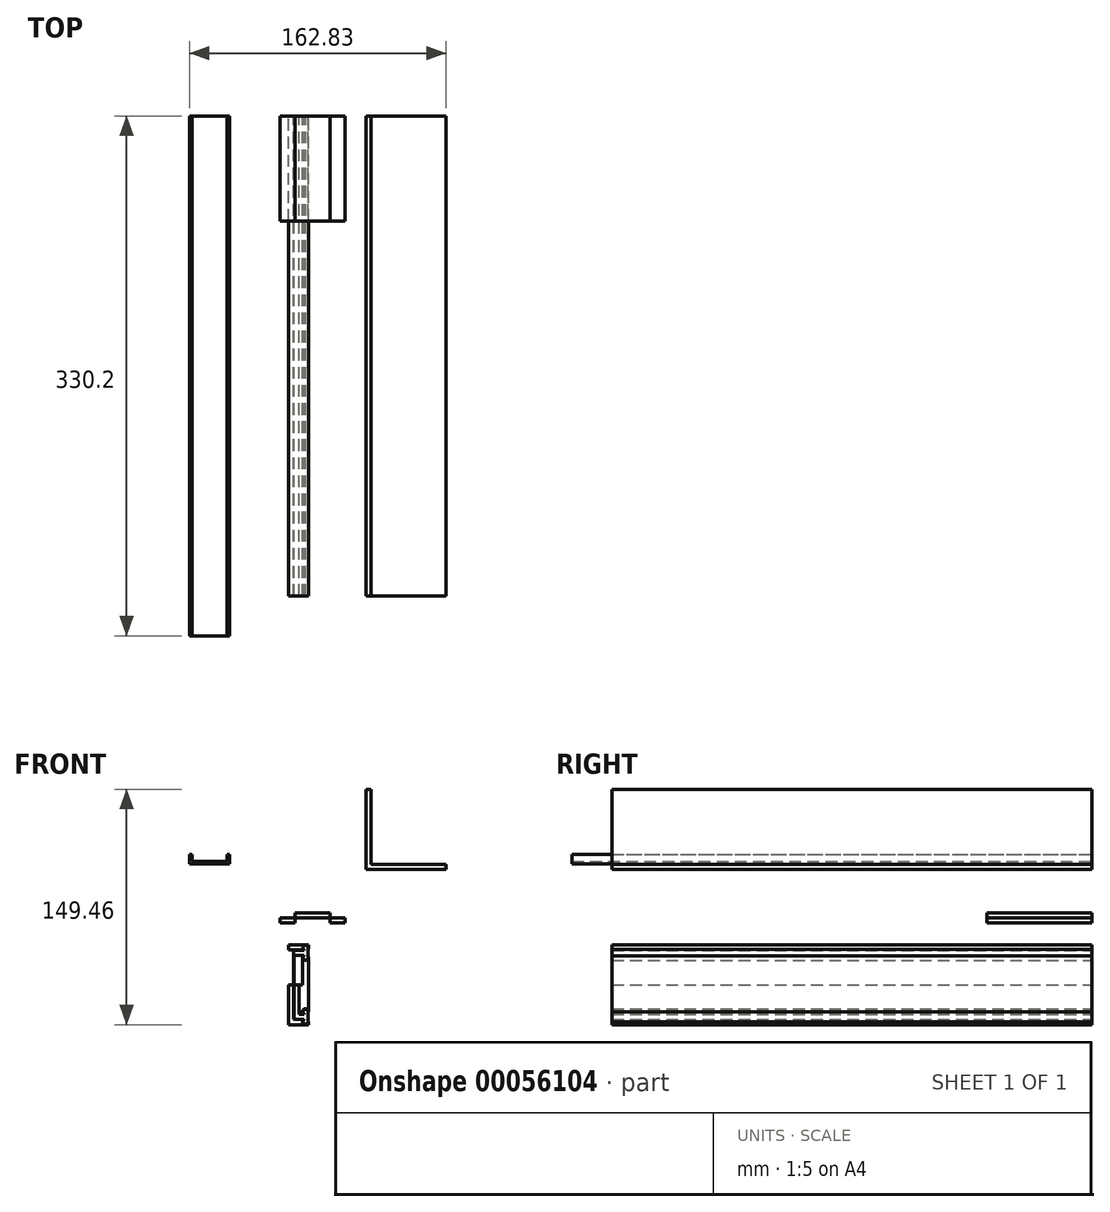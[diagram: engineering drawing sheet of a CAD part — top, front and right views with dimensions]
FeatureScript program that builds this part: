
annotation { "Feature Type Name" : "Feature", "Feature Type Description" : "" }
export const myFeature = defineFeature(function(context is Context, id is Id, definition is map)
    precondition{}
    {
        {
            var Q0;
            Q0=qCreatedBy(makeId("Front.planeOp"),FACE);
            var sketch = newSketch(context, id + "F0", { "sketchPlane" : qUnion([Q0])});
            skLineSegment(sketch, "E0.rect.bottom", {"start": v(20.64, 1.59) * mm, "end": v(-20.64, 1.59) * mm});
            skLineSegment(sketch, "E0.rect.top", {"start": v(20.64, -1.59) * mm, "end": v(-20.64, -1.59) * mm});
            skLineSegment(sketch, "E0.rect.left", {"start": v(20.64, 1.59) * mm, "end": v(20.64, -1.59) * mm});
            skLineSegment(sketch, "E0.rect.right", {"start": v(-20.64, 1.59) * mm, "end": v(-20.64, -1.59) * mm});
            skPoint(sketch, "E0.rect.middle", {"position": v(0, 0) * mm});
            skLineSegment(sketch, "E1.rect.bottom", {"start": v(11.11, 4.76) * mm, "end": v(-11.11, 4.76) * mm});
            skLineSegment(sketch, "E1.rect.top", {"start": v(11.11, -1.59) * mm, "end": v(-11.11, -1.59) * mm});
            skLineSegment(sketch, "E1.rect.left", {"start": v(11.11, 4.76) * mm, "end": v(11.11, -1.59) * mm});
            skLineSegment(sketch, "E1.rect.right", {"start": v(-11.11, 4.76) * mm, "end": v(-11.11, -1.59) * mm});
            skPoint(sketch, "E1.rect.middle", {"position": v(0, 1.59) * mm});
            skSolve(sketch);
        }
        {
            var Q0;
            {var subQ5=sQuery(id+"F0.wireOp",EDGE,"E1.rect.bottom");Q0=makeQuery(id+"F0.imprint","IMPRINT",FACE,{"disambiguationData":[TD([[makeQuery(id+"F0.imprint","IMPRINT",EDGE,{"derivedFrom":subQ5}),1.0]])]});}
            var Q1;
            {var subQ5=sQuery(id+"F0.wireOp",EDGE,"E1.rect.top");Q1=makeQuery(id+"F0.imprint","IMPRINT",FACE,{"disambiguationData":[TD([[makeQuery(id+"F0.imprint","IMPRINT",EDGE,{"derivedFrom":subQ5}),-1.0]])]});}
            var Q2;
            {var subQ0=sQuery(id+"F0.wireOp",EDGE,"E0.rect.right");Q2=makeQuery(id+"F0.imprint","IMPRINT",FACE,{"disambiguationData":[TD([[makeQuery(id+"F0.imprint","IMPRINT",EDGE,{"derivedFrom":subQ0}),1.0]])]});}
            var Q3;
            {var subQ0=sQuery(id+"F0.wireOp",EDGE,"E0.rect.left");Q3=makeQuery(id+"F0.imprint","IMPRINT",FACE,{"disambiguationData":[TD([[makeQuery(id+"F0.imprint","IMPRINT",EDGE,{"derivedFrom":subQ0}),-1.0]])]});}
            extrude(context, id + "F1", {"entities" : qUnion([Q0, Q1, Q2, Q3]), "depth" : 66.67 * mm});
        }
        {
            var Q0;
            Q0=qCreatedBy(makeId("Front.planeOp"),FACE);
            var sketch = newSketch(context, id + "F2", { "sketchPlane" : qUnion([Q0])});
            skLineSegment(sketch, "E2.rect.bottom", {"start": v(-52.61, 35.78) * mm, "end": v(-78.01, 35.78) * mm});
            skLineSegment(sketch, "E2.rect.top", {"start": v(-52.61, 41.77) * mm, "end": v(-78.01, 41.77) * mm});
            skLineSegment(sketch, "E2.rect.left", {"start": v(-52.61, 35.78) * mm, "end": v(-52.61, 41.77) * mm});
            skLineSegment(sketch, "E2.rect.right", {"start": v(-78.01, 35.78) * mm, "end": v(-78.01, 41.77) * mm});
            skPoint(sketch, "E2.rect.middle", {"position": v(-65.31, 38.77) * mm});
            skLineSegment(sketch, "E3.rect.bottom", {"start": v(-76.42, 37.36) * mm, "end": v(-54.2, 37.36) * mm});
            skLineSegment(sketch, "E3.rect.top", {"start": v(-76.42, 46.18) * mm, "end": v(-54.2, 46.18) * mm});
            skLineSegment(sketch, "E3.rect.left", {"start": v(-76.42, 37.36) * mm, "end": v(-76.42, 46.18) * mm});
            skLineSegment(sketch, "E3.rect.right", {"start": v(-54.2, 37.36) * mm, "end": v(-54.2, 46.18) * mm});
            skPoint(sketch, "E3.rect.middle", {"position": v(-65.31, 41.77) * mm});
            skSolve(sketch);
        }
        {
            var Q0;
            Q0=makeQuery(id+"F2.imprint","IMPRINT",FACE,{"disambiguationData":[TD([[makeQuery(id+"F2.imprint","IMPRINT",EDGE,{"derivedFrom":sQuery(id+"F2.wireOp",EDGE,"E2.rect.bottom")}),-1.0]])]});
            extrude(context, id + "F3", {"entities" : qUnion([Q0]), "depth" : 330.2 * mm});
        }
        {
            var Q0;
            Q0=qCreatedBy(makeId("Front.planeOp"),FACE);
            var sketch = newSketch(context, id + "F4", { "sketchPlane" : qUnion([Q0])});
            skLineSegment(sketch, "E4.bottom", {"start": v(34.02, 32.27) * mm, "end": v(84.82, 32.27) * mm});
            skLineSegment(sketch, "E4.top", {"start": v(34.02, 83.07) * mm, "end": v(84.82, 83.07) * mm});
            skLineSegment(sketch, "E4.left", {"start": v(34.02, 32.27) * mm, "end": v(34.02, 83.07) * mm});
            skLineSegment(sketch, "E4.right", {"start": v(84.82, 32.27) * mm, "end": v(84.82, 83.07) * mm});
            skLineSegment(sketch, "E5.bottom", {"start": v(37.2, 35.44) * mm, "end": v(84.82, 35.44) * mm});
            skLineSegment(sketch, "E5.top", {"start": v(37.2, 83.07) * mm, "end": v(84.82, 83.07) * mm});
            skLineSegment(sketch, "E5.left", {"start": v(37.2, 35.44) * mm, "end": v(37.2, 83.07) * mm});
            skLineSegment(sketch, "E5.right", {"start": v(84.82, 35.44) * mm, "end": v(84.82, 83.07) * mm});
            skSolve(sketch);
        }
        {
            var Q0;
            Q0=makeQuery(id+"F4.imprint","IMPRINT",FACE,{"disambiguationData":[TD([[makeQuery(id+"F4.imprint","IMPRINT",EDGE,{"derivedFrom":sQuery(id+"F4.wireOp",EDGE,"E4.bottom")}),1.0]])]});
            extrude(context, id + "F5", {"entities" : qUnion([Q0]), "depth" : 304.8 * mm});
        }
        {
            var Q0;
            Q0=qCreatedBy(makeId("Front.planeOp"),FACE);
            var sketch = newSketch(context, id + "F6", { "sketchPlane" : qUnion([Q0])});
            skLineSegment(sketch, "E6", {"start": v(0, -40.99) * mm, "end": v(-21.53, -40.99) * mm, "construction": true});
            skCircle(sketch, "E7", {"center": v(-4.4, -17.5) * mm, "radius": 1.59 * mm});
            skCircle(sketch, "E8", {"center": v(-4.4, -23.84) * mm, "radius": 1.59 * mm});
            skCircle(sketch, "E9", {"center": v(-4.4, -17.5) * mm, "radius": 1.9 * mm});
            skCircle(sketch, "E10", {"center": v(-4.4, -23.84) * mm, "radius": 1.9 * mm});
            skLineSegment(sketch, "E11.bottom", {"start": v(-2.5, -15.59) * mm, "end": v(-15.2, -15.59) * mm});
            skLineSegment(sketch, "E11.top", {"start": v(-2.5, -40.99) * mm, "end": v(-15.2, -40.99) * mm});
            skLineSegment(sketch, "E11.left", {"start": v(-2.5, -15.59) * mm, "end": v(-2.5, -40.99) * mm});
            skLineSegment(sketch, "E11.right", {"start": v(-15.2, -15.59) * mm, "end": v(-15.2, -40.99) * mm});
            skLineSegment(sketch, "E12", {"start": v(-5.82, -18.76) * mm, "end": v(-15.2, -18.76) * mm});
            skLineSegment(sketch, "E13", {"start": v(-15.2, -18.76) * mm, "end": v(-12.02, -18.76) * mm});
            skLineSegment(sketch, "E14", {"start": v(-12.02, -18.76) * mm, "end": v(-12.02, -40.99) * mm});
            skLineSegment(sketch, "E15", {"start": v(-5.45, -19.08) * mm, "end": v(-12.02, -19.08) * mm});
            skLineSegment(sketch, "E16", {"start": v(-12.02, -19.08) * mm, "end": v(-11.7, -19.08) * mm});
            skLineSegment(sketch, "E17", {"start": v(-11.7, -19.08) * mm, "end": v(-11.7, -40.99) * mm});
            skLineSegment(sketch, "E18", {"start": v(-5.45, -22.25) * mm, "end": v(-11.7, -22.25) * mm});
            skLineSegment(sketch, "E19", {"start": v(-11.7, -22.25) * mm, "end": v(-8.53, -22.25) * mm});
            skLineSegment(sketch, "E20", {"start": v(-8.53, -22.25) * mm, "end": v(-8.53, -40.99) * mm});
            skLineSegment(sketch, "E21", {"start": v(-6.3, -23.84) * mm, "end": v(-6.3, -40.99) * mm});
            skLineSegment(sketch, "E22", {"start": v(-2.5, -23.84) * mm, "end": v(-2.5, -40.99) * mm});
            skLineSegment(sketch, "E23.bottom", {"start": v(-5.45, -17.5) * mm, "end": v(-2.81, -17.5) * mm});
            skLineSegment(sketch, "E23.top", {"start": v(-5.45, -23.84) * mm, "end": v(-2.81, -23.84) * mm});
            skLineSegment(sketch, "E23.left", {"start": v(-5.45, -17.5) * mm, "end": v(-5.45, -23.84) * mm});
            skLineSegment(sketch, "E23.right", {"start": v(-2.81, -17.5) * mm, "end": v(-2.81, -23.84) * mm});
            skLineSegment(sketch, "E24.MirrorCS", {"start": v(-12.02, -62.9) * mm, "end": v(-11.7, -62.9) * mm});
            skLineSegment(sketch, "E25.MirrorCS", {"start": v(-2.5, -58.13) * mm, "end": v(-2.5, -40.99) * mm});
            skLineSegment(sketch, "E26.MirrorCS", {"start": v(-11.7, -59.72) * mm, "end": v(-8.53, -59.72) * mm});
            skLineSegment(sketch, "E27.MirrorCS", {"start": v(-2.81, -64.48) * mm, "end": v(-2.81, -58.13) * mm});
            skLineSegment(sketch, "E28.MirrorCS", {"start": v(-5.45, -62.9) * mm, "end": v(-12.02, -62.9) * mm});
            skLineSegment(sketch, "E29.MirrorCS", {"start": v(-12.02, -63.21) * mm, "end": v(-12.02, -40.99) * mm});
            skLineSegment(sketch, "E30.MirrorCS", {"start": v(-15.2, -63.21) * mm, "end": v(-12.02, -63.21) * mm});
            skLineSegment(sketch, "E31.MirrorCS", {"start": v(-8.53, -59.72) * mm, "end": v(-8.53, -40.99) * mm});
            skLineSegment(sketch, "E32.MirrorCS", {"start": v(-5.82, -63.21) * mm, "end": v(-15.2, -63.21) * mm});
            skLineSegment(sketch, "E33.MirrorCS", {"start": v(-5.45, -58.13) * mm, "end": v(-2.81, -58.13) * mm});
            skLineSegment(sketch, "E34.MirrorCS", {"start": v(-15.2, -66.39) * mm, "end": v(-15.2, -40.99) * mm});
            skLineSegment(sketch, "E35.MirrorCS", {"start": v(-6.3, -58.13) * mm, "end": v(-6.3, -40.99) * mm});
            skLineSegment(sketch, "E36.MirrorCS", {"start": v(-2.5, -66.39) * mm, "end": v(-2.5, -40.99) * mm});
            skLineSegment(sketch, "E37.MirrorCS", {"start": v(-5.45, -64.48) * mm, "end": v(-2.81, -64.48) * mm});
            skLineSegment(sketch, "E38.MirrorCS", {"start": v(-2.5, -66.39) * mm, "end": v(-15.2, -66.39) * mm});
            skCircle(sketch, "E39.MirrorC", {"center": v(-4.4, -58.13) * mm, "radius": 1.9 * mm});
            skCircle(sketch, "E40.MirrorC", {"center": v(-4.4, -64.48) * mm, "radius": 1.9 * mm});
            skCircle(sketch, "E41.MirrorC", {"center": v(-4.4, -58.13) * mm, "radius": 1.59 * mm});
            skCircle(sketch, "E42.MirrorC", {"center": v(-4.4, -64.48) * mm, "radius": 1.59 * mm});
            skLineSegment(sketch, "E43.MirrorCS", {"start": v(-5.45, -64.48) * mm, "end": v(-5.45, -58.13) * mm});
            skLineSegment(sketch, "E44.MirrorCS", {"start": v(-5.45, -59.72) * mm, "end": v(-11.7, -59.72) * mm});
            skLineSegment(sketch, "E45.MirrorCS", {"start": v(-11.7, -62.9) * mm, "end": v(-11.7, -40.99) * mm});
            skSolve(sketch);
        }
        {
            var Q0;
            {var subQ4=sQuery(id+"F6.wireOp",EDGE,"E19");Q0=makeQuery(id+"F6.imprint","IMPRINT",FACE,{"disambiguationData":[TD([[makeQuery(id+"F6.imprint","IMPRINT",EDGE,{"derivedFrom":subQ4}),-1.0]])]});}
            var Q1;
            {var subQ3=sQuery(id+"F6.wireOp",EDGE,"E15");Q1=makeQuery(id+"F6.imprint","IMPRINT",FACE,{"disambiguationData":[TD([[makeQuery(id+"F6.imprint","IMPRINT",EDGE,{"derivedFrom":subQ3}),1.0]])]});}
            var Q2;
            {var subQ1=sQuery(id+"F6.wireOp",EDGE,"E9");var subQ3=sQuery(id+"F6.wireOp",EDGE,"E23.right");var subQ4=makeQuery(id+"F6.imprint","INTERSECT",VERTEX,{"derivedFrom":[subQ1,subQ3]});Q2=makeQuery(id+"F6.imprint","IMPRINT",FACE,{"disambiguationData":[TD([[makeQuery(id+"F6.imprint","IMPRINT",EDGE,{"disambiguationData":[TD([[subQ4,-1.0]])],"derivedFrom":subQ3}),-1.0]])]});}
            var Q3;
            {var subQ1=sQuery(id+"F6.wireOp",EDGE,"E7");var subQ3=sQuery(id+"F6.wireOp",EDGE,"E23.left");var subQ4=makeQuery(id+"F6.imprint","INTERSECT",VERTEX,{"derivedFrom":[subQ1,subQ3]});Q3=makeQuery(id+"F6.imprint","IMPRINT",FACE,{"disambiguationData":[TD([[makeQuery(id+"F6.imprint","IMPRINT",EDGE,{"disambiguationData":[TD([[subQ4,-1.0]])],"derivedFrom":subQ1}),-1.0]])]});}
            var Q4;
            {var subQ0=sQuery(id+"F6.wireOp",EDGE,"E23.bottom");Q4=makeQuery(id+"F6.imprint","IMPRINT",FACE,{"disambiguationData":[TD([[makeQuery(id+"F6.imprint","IMPRINT",EDGE,{"derivedFrom":subQ0}),-1.0]])]});}
            var Q5;
            {var subQ0=sQuery(id+"F6.wireOp",EDGE,"E23.bottom");Q5=makeQuery(id+"F6.imprint","IMPRINT",FACE,{"disambiguationData":[TD([[makeQuery(id+"F6.imprint","IMPRINT",EDGE,{"derivedFrom":subQ0}),1.0]])]});}
            var Q6;
            {var subQ1=sQuery(id+"F6.wireOp",EDGE,"E8");var subQ3=sQuery(id+"F6.wireOp",EDGE,"E23.left");var subQ4=makeQuery(id+"F6.imprint","INTERSECT",VERTEX,{"derivedFrom":[subQ1,subQ3]});Q6=makeQuery(id+"F6.imprint","IMPRINT",FACE,{"disambiguationData":[TD([[makeQuery(id+"F6.imprint","IMPRINT",EDGE,{"disambiguationData":[TD([[subQ4,1.0]])],"derivedFrom":subQ1}),-1.0]])]});}
            var Q7;
            {var subQ0=sQuery(id+"F6.wireOp",EDGE,"E23.top");Q7=makeQuery(id+"F6.imprint","IMPRINT",FACE,{"disambiguationData":[TD([[makeQuery(id+"F6.imprint","IMPRINT",EDGE,{"derivedFrom":subQ0}),1.0]])]});}
            var Q8;
            {var subQ0=sQuery(id+"F6.wireOp",EDGE,"E23.top");Q8=makeQuery(id+"F6.imprint","IMPRINT",FACE,{"disambiguationData":[TD([[makeQuery(id+"F6.imprint","IMPRINT",EDGE,{"derivedFrom":subQ0}),-1.0]])]});}
            var Q9;
            {var subQ0=sQuery(id+"F6.wireOp",EDGE,"E31.MirrorCS");Q9=makeQuery(id+"F6.imprint","IMPRINT",FACE,{"disambiguationData":[TD([[makeQuery(id+"F6.imprint","IMPRINT",EDGE,{"derivedFrom":subQ0}),1.0]])]});}
            var Q10;
            {var subQ0=sQuery(id+"F6.wireOp",EDGE,"E44.MirrorCS");var subQ1=makeQuery(id+"F6.imprint","INTERSECT",VERTEX,{"derivedFrom":[sQuery(id+"F6.wireOp",EDGE,"E31.MirrorCS"),subQ0]});Q10=makeQuery(id+"F6.imprint","IMPRINT",FACE,{"disambiguationData":[TD([[makeQuery(id+"F6.imprint","IMPRINT",EDGE,{"disambiguationData":[TD([[subQ1,-1.0]])],"derivedFrom":subQ0}),1.0]])]});}
            var Q11;
            {var subQ0=sQuery(id+"F6.wireOp",EDGE,"E40.MirrorC");var subQ1=sQuery(id+"F6.wireOp",EDGE,"E27.MirrorCS");var subQ2=makeQuery(id+"F6.imprint","INTERSECT",VERTEX,{"derivedFrom":[subQ1,subQ0]});Q11=makeQuery(id+"F6.imprint","IMPRINT",FACE,{"disambiguationData":[TD([[makeQuery(id+"F6.imprint","IMPRINT",EDGE,{"disambiguationData":[TD([[subQ2,-1.0]])],"derivedFrom":subQ1}),1.0]])]});}
            var Q12;
            {var subQ1=sQuery(id+"F6.wireOp",EDGE,"E27.MirrorCS");var subQ3=sQuery(id+"F6.wireOp",EDGE,"E39.MirrorC");var subQ4=makeQuery(id+"F6.imprint","INTERSECT",VERTEX,{"derivedFrom":[subQ1,subQ3]});Q12=makeQuery(id+"F6.imprint","IMPRINT",FACE,{"disambiguationData":[TD([[makeQuery(id+"F6.imprint","IMPRINT",EDGE,{"disambiguationData":[TD([[subQ4,-1.0]])],"derivedFrom":subQ1}),1.0]])]});}
            var Q13;
            {var subQ0=sQuery(id+"F6.wireOp",EDGE,"E33.MirrorCS");Q13=makeQuery(id+"F6.imprint","IMPRINT",FACE,{"disambiguationData":[TD([[makeQuery(id+"F6.imprint","IMPRINT",EDGE,{"derivedFrom":subQ0}),-1.0]])]});}
            var Q14;
            {var subQ0=sQuery(id+"F6.wireOp",EDGE,"E33.MirrorCS");Q14=makeQuery(id+"F6.imprint","IMPRINT",FACE,{"disambiguationData":[TD([[makeQuery(id+"F6.imprint","IMPRINT",EDGE,{"derivedFrom":subQ0}),1.0]])]});}
            var Q15;
            {var subQ0=sQuery(id+"F6.wireOp",EDGE,"E37.MirrorCS");Q15=makeQuery(id+"F6.imprint","IMPRINT",FACE,{"disambiguationData":[TD([[makeQuery(id+"F6.imprint","IMPRINT",EDGE,{"derivedFrom":subQ0}),1.0]])]});}
            var Q16;
            {var subQ1=sQuery(id+"F6.wireOp",EDGE,"E27.MirrorCS");var subQ3=sQuery(id+"F6.wireOp",EDGE,"E40.MirrorC");var subQ4=makeQuery(id+"F6.imprint","INTERSECT",VERTEX,{"derivedFrom":[subQ1,subQ3]});Q16=makeQuery(id+"F6.imprint","IMPRINT",FACE,{"disambiguationData":[TD([[makeQuery(id+"F6.imprint","IMPRINT",EDGE,{"disambiguationData":[TD([[subQ4,1.0]])],"derivedFrom":subQ1}),1.0]])]});}
            var Q17;
            {var subQ0=sQuery(id+"F6.wireOp",EDGE,"E37.MirrorCS");Q17=makeQuery(id+"F6.imprint","IMPRINT",FACE,{"disambiguationData":[TD([[makeQuery(id+"F6.imprint","IMPRINT",EDGE,{"derivedFrom":subQ0}),-1.0]])]});}
            extrude(context, id + "F7", {"entities" : qUnion([Q0, Q1, Q2, Q3, Q4, Q5, Q6, Q7, Q8, Q9, Q10, Q11, Q12, Q13, Q14, Q15, Q16, Q17]), "depth" : 304.8 * mm});
        }
        {
            var Q0;
            {var subQ0=sQuery(id+"F6.wireOp",EDGE,"E12");Q0=makeQuery(id+"F6.imprint","IMPRINT",FACE,{"disambiguationData":[TD([[makeQuery(id+"F6.imprint","IMPRINT",EDGE,{"derivedFrom":subQ0}),-1.0]])]});}
            var Q1;
            {var subQ0=sQuery(id+"F6.wireOp",EDGE,"E9");var subQ4=makeQuery(id+"F6.imprint","INTERSECT",VERTEX,{"derivedFrom":[subQ0,sQuery(id+"F6.wireOp",EDGE,"E12")]});Q1=makeQuery(id+"F6.imprint","IMPRINT",FACE,{"disambiguationData":[TD([[makeQuery(id+"F6.imprint","IMPRINT",EDGE,{"disambiguationData":[TD([[subQ4,1.0]])],"derivedFrom":subQ0}),1.0]])]});}
            var Q2;
            {var subQ0=sQuery(id+"F6.wireOp",EDGE,"E11.bottom");var subQ1=sQuery(id+"F6.wireOp",EDGE,"E9");var subQ2=makeQuery(id+"F6.imprint","INTERSECT",VERTEX,{"derivedFrom":[subQ1,subQ0]});Q2=makeQuery(id+"F6.imprint","IMPRINT",FACE,{"disambiguationData":[TD([[makeQuery(id+"F6.imprint","IMPRINT",EDGE,{"disambiguationData":[TD([[subQ2,1.0]])],"derivedFrom":subQ1}),-1.0]])]});}
            var Q3;
            {var subQ1=sQuery(id+"F6.wireOp",EDGE,"E13");Q3=makeQuery(id+"F6.imprint","IMPRINT",FACE,{"disambiguationData":[TD([[makeQuery(id+"F6.imprint","IMPRINT",EDGE,{"derivedFrom":subQ1}),-1.0]])]});}
            var Q4;
            {var subQ5=sQuery(id+"F6.wireOp",EDGE,"E29.MirrorCS");var subQ6=makeQuery(id+"F6.imprint","INTERSECT",VERTEX,{"derivedFrom":[sQuery(id+"F6.wireOp",EDGE,"E28.MirrorCS"),subQ5]});Q4=makeQuery(id+"F6.imprint","IMPRINT",FACE,{"disambiguationData":[TD([[makeQuery(id+"F6.imprint","IMPRINT",EDGE,{"disambiguationData":[TD([[subQ6,1.0]])],"derivedFrom":subQ5}),1.0]])]});}
            var Q5;
            {var subQ5=sQuery(id+"F6.wireOp",EDGE,"E32.MirrorCS");var subQ7=makeQuery(id+"F6.imprint","INTERSECT",VERTEX,{"derivedFrom":[sQuery(id+"F6.wireOp",EDGE,"E29.MirrorCS"),subQ5]});Q5=makeQuery(id+"F6.imprint","IMPRINT",FACE,{"disambiguationData":[TD([[makeQuery(id+"F6.imprint","IMPRINT",EDGE,{"disambiguationData":[TD([[subQ7,1.0]])],"derivedFrom":subQ5}),1.0]])]});}
            var Q6;
            {var subQ0=sQuery(id+"F6.wireOp",EDGE,"E38.MirrorCS");var subQ1=sQuery(id+"F6.wireOp",EDGE,"E36.MirrorCS");var subQ2=makeQuery(id+"F6.imprint","INTERSECT",VERTEX,{"derivedFrom":[subQ1,subQ0]});Q6=makeQuery(id+"F6.imprint","IMPRINT",FACE,{"disambiguationData":[TD([[makeQuery(id+"F6.imprint","IMPRINT",EDGE,{"disambiguationData":[TD([[subQ2,-1.0]])],"derivedFrom":subQ1}),1.0]])]});}
            var Q7;
            {var subQ0=sQuery(id+"F6.wireOp",EDGE,"E40.MirrorC");var subQ8=makeQuery(id+"F6.imprint","INTERSECT",VERTEX,{"derivedFrom":[sQuery(id+"F6.wireOp",EDGE,"E32.MirrorCS"),subQ0]});Q7=makeQuery(id+"F6.imprint","IMPRINT",FACE,{"disambiguationData":[TD([[makeQuery(id+"F6.imprint","IMPRINT",EDGE,{"disambiguationData":[TD([[subQ8,1.0]])],"derivedFrom":subQ0}),-1.0]])]});}
            extrude(context, id + "F8", {"entities" : qUnion([Q0, Q1, Q2, Q3, Q4, Q5, Q6, Q7]), "depth" : 304.8 * mm});
        }
        {
            var Q0;
            {var subQ2=sQuery(id+"F6.wireOp",EDGE,"E21");Q0=makeQuery(id+"F6.imprint","IMPRINT",FACE,{"disambiguationData":[TD([[makeQuery(id+"F6.imprint","IMPRINT",EDGE,{"derivedFrom":subQ2}),1.0]])]});}
            var Q1;
            {var subQ5=sQuery(id+"F6.wireOp",EDGE,"E23.left");var subQ7=sQuery(id+"F6.wireOp",EDGE,"E8");var subQ8=makeQuery(id+"F6.imprint","INTERSECT",VERTEX,{"derivedFrom":[subQ7,subQ5]});Q1=makeQuery(id+"F6.imprint","IMPRINT",FACE,{"disambiguationData":[TD([[makeQuery(id+"F6.imprint","IMPRINT",EDGE,{"disambiguationData":[TD([[subQ8,-1.0]])],"derivedFrom":subQ7}),-1.0]])]});}
            var Q2;
            {var subQ0=sQuery(id+"F6.wireOp",EDGE,"E35.MirrorCS");Q2=makeQuery(id+"F6.imprint","IMPRINT",FACE,{"disambiguationData":[TD([[makeQuery(id+"F6.imprint","IMPRINT",EDGE,{"derivedFrom":subQ0}),-1.0]])]});}
            var Q3;
            {var subQ0=sQuery(id+"F6.wireOp",EDGE,"E39.MirrorC");var subQ4=makeQuery(id+"F6.imprint","INTERSECT",VERTEX,{"derivedFrom":[sQuery(id+"F6.wireOp",EDGE,"E35.MirrorCS"),subQ0]});Q3=makeQuery(id+"F6.imprint","IMPRINT",FACE,{"disambiguationData":[TD([[makeQuery(id+"F6.imprint","IMPRINT",EDGE,{"disambiguationData":[TD([[subQ4,-1.0]])],"derivedFrom":subQ0}),-1.0]])]});}
            extrude(context, id + "F9", {"entities" : qUnion([Q0, Q1, Q2, Q3]), "depth" : 304.8 * mm});
        }
    });
